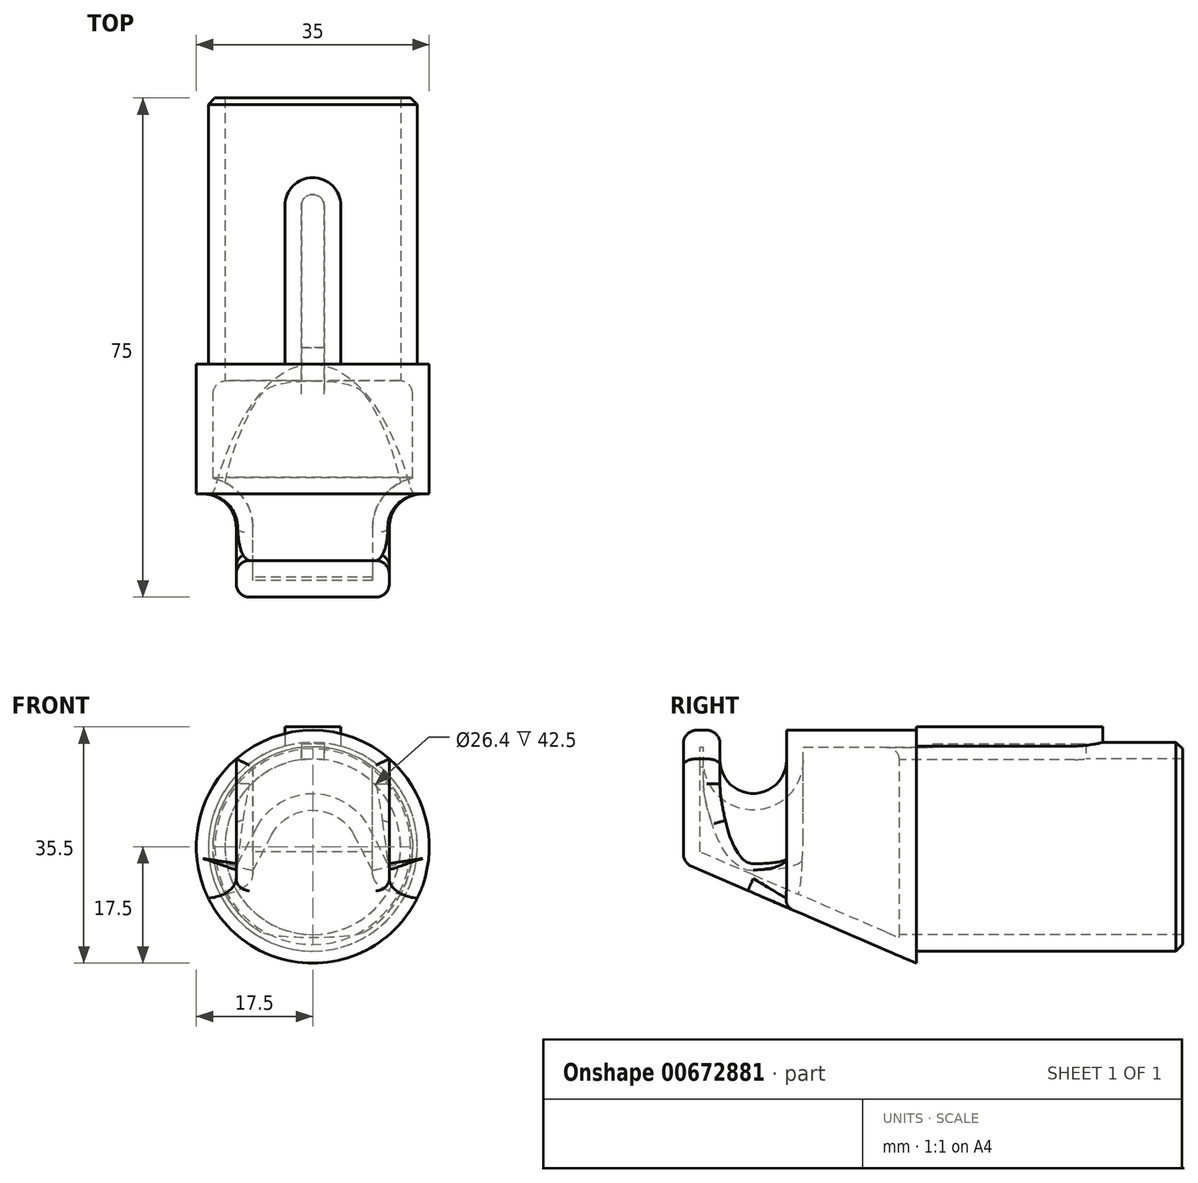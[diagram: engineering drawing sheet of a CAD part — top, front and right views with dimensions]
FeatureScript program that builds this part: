
annotation { "Feature Type Name" : "Feature", "Feature Type Description" : "" }
export const myFeature = defineFeature(function(context is Context, id is Id, definition is map)
    precondition{}
    {
        {
            var Q0;
            Q0=qCreatedBy(makeId("Front.planeOp"),FACE);
            var sketch = newSketch(context, id + "F0", { "sketchPlane" : qUnion([Q0])});
            skArc(sketch, "E0", {"start": v(0, -15.7) * mm, "mid": v(15.7, 0) * mm, "end": v(0, 15.7) * mm});
            skLineSegment(sketch, "E1", {"start": v(0, 15.7) * mm, "end": v(0, -15.7) * mm});
            skSolve(sketch);
        }
        {
            var Q0;
            Q0 = qSketchRegion(id + "F0", true);
            extrude(context, id + "F1", {"entities" : qUnion([Q0]), "oppositeDirection" : true, "depth" : 40 * mm, "offsetDistance" : 25 * mm});
        }
        {
            var Q0;
            Q0=qCreatedBy(makeId("Top.planeOp"),FACE);
            var sketch = newSketch(context, id + "F2", { "sketchPlane" : qUnion([Q0])});
            skLineSegment(sketch, "E2.bottom", {"start": v(0, 0) * mm, "end": v(4.2, 0) * mm});
            skLineSegment(sketch, "E2.right", {"start": v(4.2, 0) * mm, "end": v(4.2, 23.8) * mm});
            skArc(sketch, "E3", {"start": v(4.2, 23.8) * mm, "mid": v(2.97, 26.77) * mm, "end": v(0, 28) * mm});
            skLineSegment(sketch, "E4", {"start": v(0, 28) * mm, "end": v(0, 0) * mm});
            skSolve(sketch);
        }
        {
            var Q0;
            Q0 = qSketchRegion(id + "F2", true);
            extrude(context, id + "F3", {"entities" : qUnion([Q0]), "operationType" : NewBodyOperationType.ADD, "depth" : 18 * mm, "offsetDistance" : 25 * mm});
        }
        {
            var Q0;
            Q0=qCreatedBy(makeId("Front.planeOp"),FACE);
            var sketch = newSketch(context, id + "F4", { "sketchPlane" : qUnion([Q0])});
            skArc(sketch, "E5", {"start": v(0, -17.5) * mm, "mid": v(17.5, 0) * mm, "end": v(0, 17.5) * mm});
            skLineSegment(sketch, "E6.bottom", {"start": v(0, 10) * mm, "end": v(14.36, 10) * mm, "construction": true});
            skLineSegment(sketch, "E6.top", {"start": v(0, -10) * mm, "end": v(14.36, -10) * mm, "construction": true});
            skLineSegment(sketch, "E6.right", {"start": v(14.36, 10) * mm, "end": v(14.36, -10) * mm, "construction": true});
            skLineSegment(sketch, "E7", {"start": v(0, 17.5) * mm, "end": v(0, -17.5) * mm});
            skPoint(sketch, "E7.endSnap0", {"position": v(0, -10) * mm});
            skSolve(sketch);
        }
        {
            var Q0;
            Q0=qCreatedBy(makeId("Right.planeOp"),FACE);
            var sketch = newSketch(context, id + "F5", { "sketchPlane" : qUnion([Q0])});
            skLineSegment(sketch, "E8", {"start": v(-31, 13) * mm, "end": v(-31, 18) * mm});
            skLineSegment(sketch, "E9", {"start": v(-31, 18) * mm, "end": v(-39, 18) * mm});
            skLineSegment(sketch, "E10", {"start": v(-10, 13) * mm, "end": v(-10, 18) * mm});
            skLineSegment(sketch, "E11", {"start": v(-10, 18) * mm, "end": v(-18, 18) * mm});
            skLineSegment(sketch, "E12", {"start": v(-18, 18) * mm, "end": v(-18, 13) * mm});
            skArc(sketch, "E13", {"start": v(-31, 13) * mm, "mid": v(-24.5, 6.5) * mm, "end": v(-18, 13) * mm});
            skLineSegment(sketch, "E14", {"start": v(-39, 18) * mm, "end": v(-39, 13) * mm});
            skLineSegment(sketch, "E15", {"start": v(-39, 13) * mm, "end": v(-29, -2) * mm});
            skLineSegment(sketch, "E16", {"start": v(-29, -2) * mm, "end": v(-10, 13) * mm});
            skSolve(sketch);
        }
        {
            var Q0;
            Q0=sQuery(id+"F5.wireOp",VERTEX,"E13.center");
            var Q1;
            Q1=qCreatedBy(makeId("Front.planeOp"),FACE);
            cPlane(context, id + "F6", {"entities" : qUnion([Q0, Q1]), "cplaneType" : CPlaneType.PLANE_POINT, "offset" : 25 * mm, "width" : 150 * mm, "height" : 150 * mm});
        }
        {
            var Q0;
            Q0=qCreatedBy(id+"F6.planeOp",FACE);
            var sketch = newSketch(context, id + "F7", { "sketchPlane" : qUnion([Q0])});
            skLineSegment(sketch, "E17", {"start": v(0, -9) * mm, "end": v(11.5, -9) * mm});
            skLineSegment(sketch, "E18", {"start": v(11.5, -9) * mm, "end": v(11.5, -3) * mm});
            skLineSegment(sketch, "E19", {"start": v(11.5, -3) * mm, "end": v(8.42, 2.9) * mm});
            skArc(sketch, "E20", {"start": v(8.42, 2.9) * mm, "mid": v(4.92, 6.62) * mm, "end": v(0, 8) * mm});
            skLineSegment(sketch, "E21", {"start": v(0, 8) * mm, "end": v(0, -9) * mm});
            skSolve(sketch);
        }
        {
            var Q0;
            Q0 = qSketchRegion(id + "F4", true);
            extrude(context, id + "F8", {"entities" : qUnion([Q0]), "operationType" : NewBodyOperationType.ADD, "depth" : 35 * mm, "offsetDistance" : 25 * mm});
        }
        {
            var Q0;
            Q0=qCreatedBy(makeId("Top.planeOp"),FACE);
            var Q1;
            Q1=sQuery(id+"F7.wireOp",VERTEX,"E17.end");
            cPlane(context, id + "F9", {"entities" : qUnion([Q0, Q1]), "cplaneType" : CPlaneType.PLANE_POINT, "offset" : 25 * mm, "width" : 150 * mm, "height" : 150 * mm});
        }
        {
            var Q0;
            Q0=qCreatedBy(id+"F9.planeOp",FACE);
            var sketch = newSketch(context, id + "F10", { "sketchPlane" : qUnion([Q0])});
            skArc(sketch, "E22", {"start": v(16.5, -19.5) * mm, "mid": v(11.5, -24.5) * mm, "end": v(16.5, -29.5) * mm});
            skLineSegment(sketch, "E23", {"start": v(16.5, -19.5) * mm, "end": v(24.5, -19.5) * mm});
            skLineSegment(sketch, "E24", {"start": v(24.5, -19.5) * mm, "end": v(24.5, -29.5) * mm});
            skLineSegment(sketch, "E25", {"start": v(24.5, -29.5) * mm, "end": v(16.5, -29.5) * mm});
            skSolve(sketch);
        }
        {
            var Q0;
            Q0=makeQuery(id+"F10.imprint","IMPRINT",FACE,{"disambiguationData":[TD([[makeQuery(id+"F10.imprint","IMPRINT",EDGE,{"derivedFrom":sQuery(id+"F10.wireOp",EDGE,"E22")}),1.0]])]});
            var Q1;
            Q1=sQuery(id+"F7.wireOp",EDGE,"E18");
            var Q2;
            Q2=sQuery(id+"F7.wireOp",EDGE,"E19");
            var Q3;
            Q3=sQuery(id+"F7.wireOp",EDGE,"E20");
            sweep(context, id + "F11", {"operationType" : NewBodyOperationType.REMOVE, "profiles" : qUnion([Q0]), "path" : qUnion([Q1, Q2, Q3])});
        }
        {
            var Q0;
            Q0=qCreatedBy(id+"F6.planeOp",FACE);
            var sketch = newSketch(context, id + "F12", { "sketchPlane" : qUnion([Q0])});
            skLineSegment(sketch, "E26", {"start": v(0, -9) * mm, "end": v(11.5, -9) * mm});
            skLineSegment(sketch, "E27", {"start": v(11.5, -9) * mm, "end": v(11.5, 13.2) * mm});
            skArc(sketch, "E28.0", {"start": v(11.5, 13.2) * mm, "mid": v(6.14, 16.39) * mm, "end": v(0, 17.5) * mm});
            skPoint(sketch, "E29.orphan", {"position": v(0, -17.5) * mm});
            skLineSegment(sketch, "E30", {"start": v(0, -9) * mm, "end": v(0, -20.46) * mm});
            skLineSegment(sketch, "E31", {"start": v(0, -20.46) * mm, "end": v(27, -20.46) * mm});
            skLineSegment(sketch, "E32", {"start": v(27, -20.46) * mm, "end": v(27, 20.46) * mm});
            skLineSegment(sketch, "E33", {"start": v(27, 20.46) * mm, "end": v(0, 20.46) * mm});
            skLineSegment(sketch, "E34", {"start": v(0, 20.46) * mm, "end": v(0, 17.5) * mm});
            skSolve(sketch);
        }
        {
            var Q0;
            Q0 = qSketchRegion(id + "F12", true);
            extrude(context, id + "F13", {"entities" : qUnion([Q0]), "operationType" : NewBodyOperationType.REMOVE, "depth" : 25 * mm, "offsetDistance" : 25 * mm});
        }
        {
            var Q0;
            Q0=qCreatedBy(makeId("Right.planeOp"),FACE);
            var sketch = newSketch(context, id + "F14", { "sketchPlane" : qUnion([Q0])});
            skLineSegment(sketch, "E35", {"start": v(-35, -2.42) * mm, "end": v(0, -17.5) * mm});
            skLineSegment(sketch, "E36", {"start": v(0, -17.5) * mm, "end": v(0, -22.76) * mm});
            skLineSegment(sketch, "E37", {"start": v(0, -22.76) * mm, "end": v(-43.04, -22.76) * mm});
            skLineSegment(sketch, "E38", {"start": v(-43.04, -22.76) * mm, "end": v(-43.04, -2.3) * mm});
            skLineSegment(sketch, "E39", {"start": v(-43.04, -2.3) * mm, "end": v(-35, -2.42) * mm});
            skSolve(sketch);
        }
        {
            var Q0;
            Q0 = qSketchRegion(id + "F14", true);
            extrude(context, id + "F15", {"entities" : qUnion([Q0]), "operationType" : NewBodyOperationType.REMOVE, "endBound" : BoundingType.SYMMETRIC, "oppositeDirection" : true, "depth" : 50 * mm, "offsetDistance" : 25 * mm});
        }
        {
            var Q0;
            Q0=makeQuery(id+"F1.opExtrude","SWEPT_BODY",BODY,{"disambiguationData":[OSD([sQuery(id+"F0.wireOp",EDGE,"E0"),sQuery(id+"F0.wireOp",EDGE,"E1")])]});
            var Q1;
            Q1=qCreatedBy(makeId("Right.planeOp"),FACE);
            mirror(context, id + "F16", {"operationType" : NewBodyOperationType.ADD, "entities" : qUnion([Q0]), "mirrorPlane" : qUnion([Q1])});
        }
        {
            var Q0;
            Q0=makeQuery(id+"F16.opPattern","COPY",EDGE,{"derivedFrom":makeQuery(id+"F13.boolean.opBoolean","INTERSECT",EDGE,{"derivedFrom":[makeQuery(id+"F8.opExtrude","CAP_FACE",FACE,{"disambiguationData":[OSD([sQuery(id+"F4.wireOp",EDGE,"E5"),sQuery(id+"F4.wireOp",EDGE,"E7")])],"isStart":false}),makeQuery(id+"F13.opExtrude","SWEPT_FACE",FACE,{"disambiguationData":[OSD([sQuery(id+"F12.wireOp",EDGE,"E27")])]})]}),"instanceName":"1"});
            var Q1;
            {var subQ0=makeQuery(id+"F15.boolean.opBoolean","COPY",EDGE,{"derivedFrom":makeQuery(id+"F15.opExtrude","SWEPT_EDGE",EDGE,{"disambiguationData":[OSD([sQuery(id+"F14.wireOp",EDGE,"E35"),sQuery(id+"F14.wireOp",EDGE,"E39")])]})});Q1=makeQuery(id+"F16.boolean.opBoolean","MERGE",EDGE,{"derivedFrom":[subQ0,makeQuery(id+"F16.opPattern","COPY",EDGE,{"derivedFrom":subQ0,"instanceName":"1"})]});}
            var Q2;
            Q2=makeQuery(id+"F13.boolean.opBoolean","INTERSECT",EDGE,{"derivedFrom":[makeQuery(id+"F8.opExtrude","CAP_FACE",FACE,{"disambiguationData":[OSD([sQuery(id+"F4.wireOp",EDGE,"E5"),sQuery(id+"F4.wireOp",EDGE,"E7")])],"isStart":false}),makeQuery(id+"F13.opExtrude","SWEPT_FACE",FACE,{"disambiguationData":[OSD([sQuery(id+"F12.wireOp",EDGE,"E27")])]})]});
            var Q3;
            {var subQ0=makeQuery(id+"F8.opExtrude","CAP_FACE",FACE,{"disambiguationData":[OSD([sQuery(id+"F4.wireOp",EDGE,"E5"),sQuery(id+"F4.wireOp",EDGE,"E7")])],"isStart":false});Q3=makeQuery(id+"F16.boolean.opBoolean","MERGE",FACE,{"derivedFrom":[subQ0,makeQuery(id+"F16.opPattern","COPY",FACE,{"derivedFrom":subQ0,"instanceName":"1"})]});}
            var Q4;
            {var subQ0=makeQuery(id+"F11.boolean.opBoolean","INTERSECT",EDGE,{"derivedFrom":[makeQuery(id+"F8.opExtrude","SWEPT_FACE",FACE,{"disambiguationData":[OSD([sQuery(id+"F4.wireOp",EDGE,"E5")])]}),makeQuery(id+"F11.opSweep","SWEPT_FACE",FACE,{"disambiguationData":[OSD([sQuery(id+"F7.wireOp",EDGE,"E18"),sQuery(id+"F10.wireOp",EDGE,"E25")])]})]});Q4=makeQuery(id+"F16.boolean.opBoolean","MERGE",EDGE,{"derivedFrom":[subQ0,makeQuery(id+"F16.opPattern","COPY",EDGE,{"derivedFrom":subQ0,"instanceName":"1"})]});}
            var Q5;
            Q5=makeQuery(id+"F16.opPattern","COPY",EDGE,{"derivedFrom":makeQuery(id+"F13.boolean.opBoolean","INTERSECT",EDGE,{"derivedFrom":[makeQuery(id+"F11.boolean.opBoolean","COPY",FACE,{"derivedFrom":makeQuery(id+"F11.opSweep","SWEPT_FACE",FACE,{"disambiguationData":[OSD([sQuery(id+"F7.wireOp",EDGE,"E18"),sQuery(id+"F10.wireOp",EDGE,"E25")])]})}),makeQuery(id+"F13.opExtrude","SWEPT_FACE",FACE,{"disambiguationData":[OSD([sQuery(id+"F12.wireOp",EDGE,"E27")])]})]}),"instanceName":"1"});
            var Q6;
            Q6=makeQuery(id+"F13.boolean.opBoolean","INTERSECT",EDGE,{"derivedFrom":[makeQuery(id+"F11.boolean.opBoolean","COPY",FACE,{"derivedFrom":makeQuery(id+"F11.opSweep","SWEPT_FACE",FACE,{"disambiguationData":[OSD([sQuery(id+"F7.wireOp",EDGE,"E18"),sQuery(id+"F10.wireOp",EDGE,"E25")])]})}),makeQuery(id+"F13.opExtrude","SWEPT_FACE",FACE,{"disambiguationData":[OSD([sQuery(id+"F12.wireOp",EDGE,"E27")])]})]});
            var Q7;
            Q7=makeQuery(id+"F16.opPattern","COPY",EDGE,{"derivedFrom":makeQuery(id+"F15.boolean.opBoolean","INTERSECT",EDGE,{"derivedFrom":[makeQuery(id+"F13.boolean.opBoolean","COPY",FACE,{"derivedFrom":makeQuery(id+"F13.opExtrude","SWEPT_FACE",FACE,{"disambiguationData":[OSD([sQuery(id+"F12.wireOp",EDGE,"E27")])]})}),makeQuery(id+"F15.opExtrude","SWEPT_FACE",FACE,{"disambiguationData":[OSD([sQuery(id+"F14.wireOp",EDGE,"E35")])]})]}),"instanceName":"1"});
            var Q8;
            Q8=makeQuery(id+"F15.boolean.opBoolean","INTERSECT",EDGE,{"derivedFrom":[makeQuery(id+"F13.boolean.opBoolean","COPY",FACE,{"derivedFrom":makeQuery(id+"F13.opExtrude","SWEPT_FACE",FACE,{"disambiguationData":[OSD([sQuery(id+"F12.wireOp",EDGE,"E27")])]})}),makeQuery(id+"F15.opExtrude","SWEPT_FACE",FACE,{"disambiguationData":[OSD([sQuery(id+"F14.wireOp",EDGE,"E35")])]})]});
            var Q9;
            Q9=makeQuery(id+"F13.boolean.opBoolean","COPY",EDGE,{"derivedFrom":makeQuery(id+"F13.opExtrude","SWEPT_EDGE",EDGE,{"disambiguationData":[OSD([sQuery(id+"F12.wireOp",EDGE,"E27"),sQuery(id+"F12.wireOp",EDGE,"E28.0")])]})});
            var Q10;
            Q10=makeQuery(id+"F16.opPattern","COPY",EDGE,{"derivedFrom":makeQuery(id+"F13.boolean.opBoolean","COPY",EDGE,{"derivedFrom":makeQuery(id+"F13.opExtrude","SWEPT_EDGE",EDGE,{"disambiguationData":[OSD([sQuery(id+"F12.wireOp",EDGE,"E27"),sQuery(id+"F12.wireOp",EDGE,"E28.0")])]})}),"instanceName":"1"});
            fillet(context, id + "F17", {"entities" : qUnion([Q0, Q1, Q2, Q3, Q4, Q5, Q6, Q7, Q8, Q9, Q10]), "radius" : 2 * mm, "tangentPropagation" : true, "allowEdgeOverflow" : false});
        }
        {
            var Q0;
            {var subQ0=makeQuery(id+"F1.opExtrude","CAP_FACE",FACE,{"disambiguationData":[OSD([sQuery(id+"F0.wireOp",EDGE,"E0"),sQuery(id+"F0.wireOp",EDGE,"E1")])],"isStart":false});Q0=makeQuery(id+"F16.boolean.opBoolean","MERGE",FACE,{"derivedFrom":[subQ0,makeQuery(id+"F16.opPattern","COPY",FACE,{"derivedFrom":subQ0,"instanceName":"1"})]});}
            shell(context, id + "F18", {"entities" : qUnion([Q0]), "thickness" : 2.5 * mm});
        }
        {
            var Q0;
            {var subQ0=makeQuery(id+"F1.opExtrude","CAP_EDGE",EDGE,{"disambiguationData":[OSD([sQuery(id+"F0.wireOp",EDGE,"E0")])],"isStart":false});Q0=makeQuery(id+"F16.boolean.opBoolean","MERGE",EDGE,{"derivedFrom":[subQ0,makeQuery(id+"F16.opPattern","COPY",EDGE,{"derivedFrom":subQ0,"instanceName":"1"})]});}
            chamfer(context, id + "F19", {"entities" : qUnion([Q0]), "width" : 1 * mm, "tangentPropagation" : true});
        }
        {
            var Q0;
            {var subQ0=sQuery(id+"F4.wireOp",EDGE,"E5");Q0=makeQuery(id+"F18.opShell","OFFSET_EDGE",EDGE,{"disambiguationData":[OSD([subQ0]),TDD([makeQuery(id+"F16.opPattern","COPY",EDGE,{"derivedFrom":makeQuery(id+"F8.boolean.opBoolean","SPLIT",EDGE,{"disambiguationData":[topologyDisambiguationEdgeConnected([makeQuery(id+"F8.opExtrude","CAP_FACE",FACE,{"disambiguationData":[OSD([subQ0,sQuery(id+"F4.wireOp",EDGE,"E7")])],"isStart":true})])],"derivedFrom":makeQuery(id+"F8.opExtrude","CAP_EDGE",EDGE,{"disambiguationData":[OSD([subQ0])],"isStart":true})}),"instanceName":"1"})])]});}
            fillet(context, id + "F20", {"entities" : qUnion([Q0]), "radius" : 2 * mm, "tangentPropagation" : true, "allowEdgeOverflow" : false});
        }
    });
